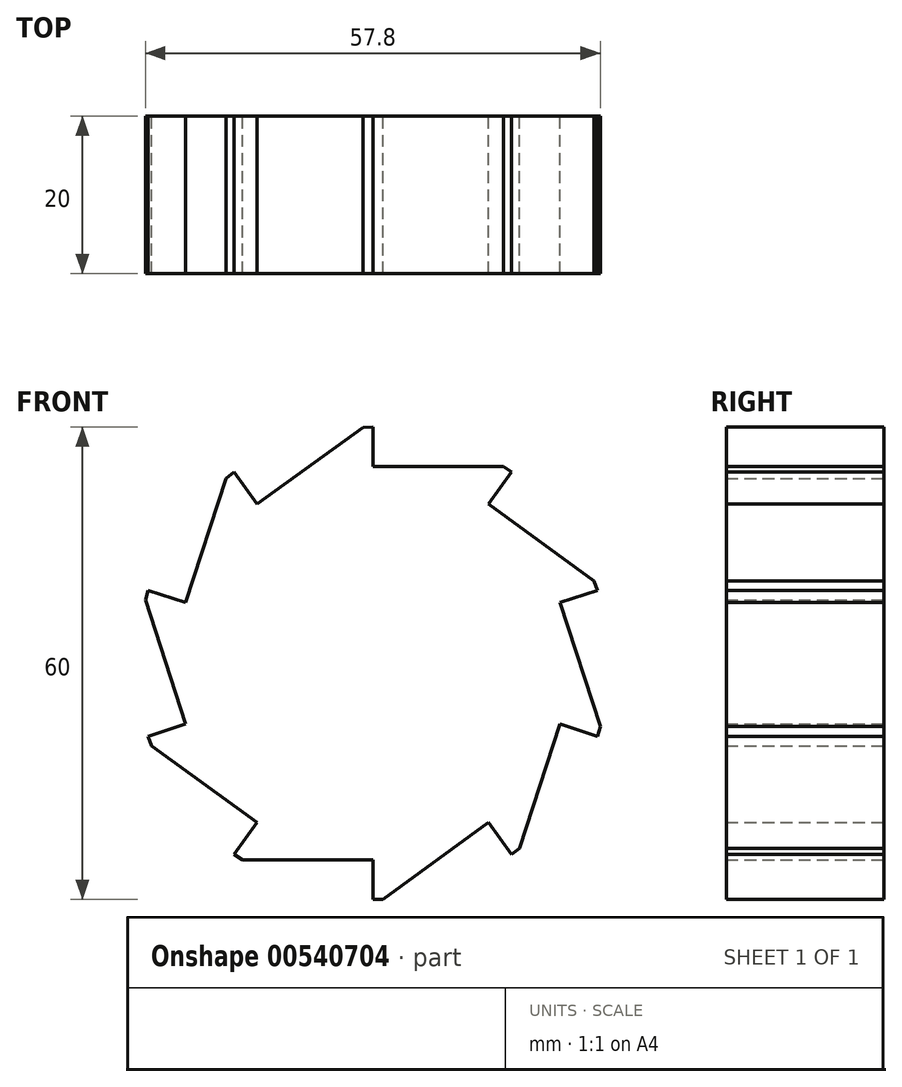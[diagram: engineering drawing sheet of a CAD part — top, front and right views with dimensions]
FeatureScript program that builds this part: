
annotation { "Feature Type Name" : "Feature", "Feature Type Description" : "" }
export const myFeature = defineFeature(function(context is Context, id is Id, definition is map)
    precondition{}
    {
        {
            var Q0;
            Q0=qCreatedBy(makeId("Front.planeOp"),FACE);
            var sketch = newSketch(context, id + "F0", { "sketchPlane" : qUnion([Q0])});
            skCircle(sketch, "E0", {"center": v(0, 0) * mm, "radius": 30 * mm});
            skPoint(sketch, "E1", {"position": v(0, 30) * mm});
            skLineSegment(sketch, "E2", {"start": v(0, 30) * mm, "end": v(0, 25) * mm});
            skLineSegment(sketch, "E3", {"start": v(0, 25) * mm, "end": v(16.58, 25) * mm});
            skLineSegment(sketch, "E4", {"start": v(0, 30) * mm, "end": v(-1.28, 29.97) * mm});
            skLineSegment(sketch, "E5.1.0", {"start": v(-17.63, 24.27) * mm, "end": v(-18.65, 23.5) * mm});
            skLineSegment(sketch, "E5.1.1", {"start": v(-17.63, 24.27) * mm, "end": v(-14.7, 20.23) * mm});
            skLineSegment(sketch, "E5.1.2", {"start": v(-14.7, 20.23) * mm, "end": v(-1.28, 29.97) * mm});
            skLineSegment(sketch, "E5.2.0", {"start": v(-28.53, 9.27) * mm, "end": v(-28.9, 8.05) * mm});
            skLineSegment(sketch, "E5.2.1", {"start": v(-28.53, 9.27) * mm, "end": v(-23.78, 7.73) * mm});
            skLineSegment(sketch, "E5.2.2", {"start": v(-23.78, 7.73) * mm, "end": v(-18.65, 23.5) * mm});
            skLineSegment(sketch, "E6.2.3.0", {"start": v(-28.53, -9.27) * mm, "end": v(-28.11, -10.48) * mm});
            skLineSegment(sketch, "E6.3.3.0", {"start": v(-28.53, -9.27) * mm, "end": v(-23.78, -7.73) * mm});
            skLineSegment(sketch, "E6.6.3.0", {"start": v(-23.78, -7.73) * mm, "end": v(-28.9, 8.05) * mm});
            skLineSegment(sketch, "E6.2.4.0", {"start": v(-17.63, -24.27) * mm, "end": v(-16.58, -25) * mm});
            skLineSegment(sketch, "E6.3.4.0", {"start": v(-17.63, -24.27) * mm, "end": v(-14.7, -20.23) * mm});
            skLineSegment(sketch, "E6.6.4.0", {"start": v(-14.7, -20.23) * mm, "end": v(-28.11, -10.48) * mm});
            skLineSegment(sketch, "E6.2.5.0", {"start": v(0, -30) * mm, "end": v(1.28, -29.97) * mm});
            skLineSegment(sketch, "E6.3.5.0", {"start": v(0, -30) * mm, "end": v(0, -25) * mm});
            skLineSegment(sketch, "E6.6.5.0", {"start": v(0, -25) * mm, "end": v(-16.58, -25) * mm});
            skLineSegment(sketch, "E6.2.6.0", {"start": v(17.63, -24.27) * mm, "end": v(18.65, -23.5) * mm});
            skLineSegment(sketch, "E6.3.6.0", {"start": v(17.63, -24.27) * mm, "end": v(14.7, -20.23) * mm});
            skLineSegment(sketch, "E6.6.6.0", {"start": v(14.7, -20.23) * mm, "end": v(1.28, -29.97) * mm});
            skLineSegment(sketch, "E6.2.7.0", {"start": v(28.53, -9.27) * mm, "end": v(28.9, -8.05) * mm});
            skLineSegment(sketch, "E6.3.7.0", {"start": v(28.53, -9.27) * mm, "end": v(23.78, -7.73) * mm});
            skLineSegment(sketch, "E6.6.7.0", {"start": v(23.78, -7.73) * mm, "end": v(18.65, -23.5) * mm});
            skLineSegment(sketch, "E6.2.8.0", {"start": v(28.53, 9.27) * mm, "end": v(28.11, 10.48) * mm});
            skLineSegment(sketch, "E6.3.8.0", {"start": v(28.53, 9.27) * mm, "end": v(23.78, 7.73) * mm});
            skLineSegment(sketch, "E6.6.8.0", {"start": v(23.78, 7.73) * mm, "end": v(28.9, -8.05) * mm});
            skLineSegment(sketch, "E6.2.9.0", {"start": v(17.63, 24.27) * mm, "end": v(16.58, 25) * mm});
            skLineSegment(sketch, "E6.3.9.0", {"start": v(17.63, 24.27) * mm, "end": v(14.7, 20.23) * mm});
            skLineSegment(sketch, "E6.6.9.0", {"start": v(14.7, 20.23) * mm, "end": v(28.11, 10.48) * mm});
            skSolve(sketch);
        }
        {
            var Q0;
            Q0=makeQuery(id+"F0.imprint","IMPRINT",FACE,{"disambiguationData":[TD([[makeQuery(id+"F0.imprint","IMPRINT",EDGE,{"derivedFrom":sQuery(id+"F0.wireOp",EDGE,"E2")}),-1.0]])]});
            extrude(context, id + "F1", {"entities" : qUnion([Q0]), "depth" : 20 * mm, "offsetDistance" : 25 * mm});
        }
    });
